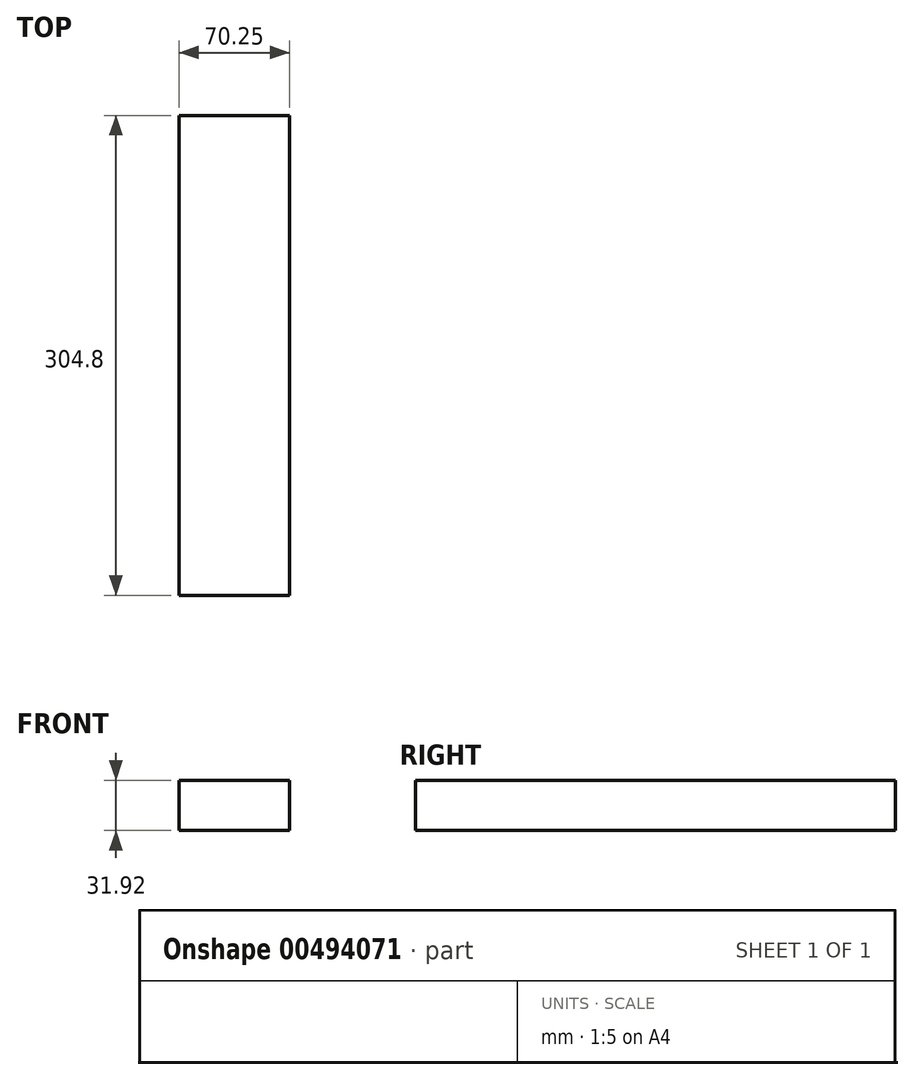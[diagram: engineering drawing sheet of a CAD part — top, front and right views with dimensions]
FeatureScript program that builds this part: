
annotation { "Feature Type Name" : "Feature", "Feature Type Description" : "" }
export const myFeature = defineFeature(function(context is Context, id is Id, definition is map)
    precondition{}
    {
        {
            var Q0;
            Q0=qCreatedBy(makeId("Front.planeOp"),FACE);
            var sketch = newSketch(context, id + "F0", { "sketchPlane" : qUnion([Q0])});
            skLineSegment(sketch, "E0.bottom", {"start": v(0, 0) * mm, "end": v(-70.25, 0) * mm});
            skLineSegment(sketch, "E0.top", {"start": v(0, 31.92) * mm, "end": v(-70.25, 31.92) * mm});
            skLineSegment(sketch, "E0.left", {"start": v(0, 0) * mm, "end": v(0, 31.92) * mm});
            skLineSegment(sketch, "E0.right", {"start": v(-70.25, 0) * mm, "end": v(-70.25, 31.92) * mm});
            skSolve(sketch);
        }
        {
            var Q0;
            Q0=makeQuery(id+"F0.imprint","IMPRINT",FACE,{"disambiguationData":[TD([[makeQuery(id+"F0.imprint","IMPRINT",EDGE,{"derivedFrom":sQuery(id+"F0.wireOp",EDGE,"E0.bottom")}),-1.0]])]});
            extrude(context, id + "F1", {"entities" : qUnion([Q0]), "depth" : 304.8 * mm});
        }
    });
